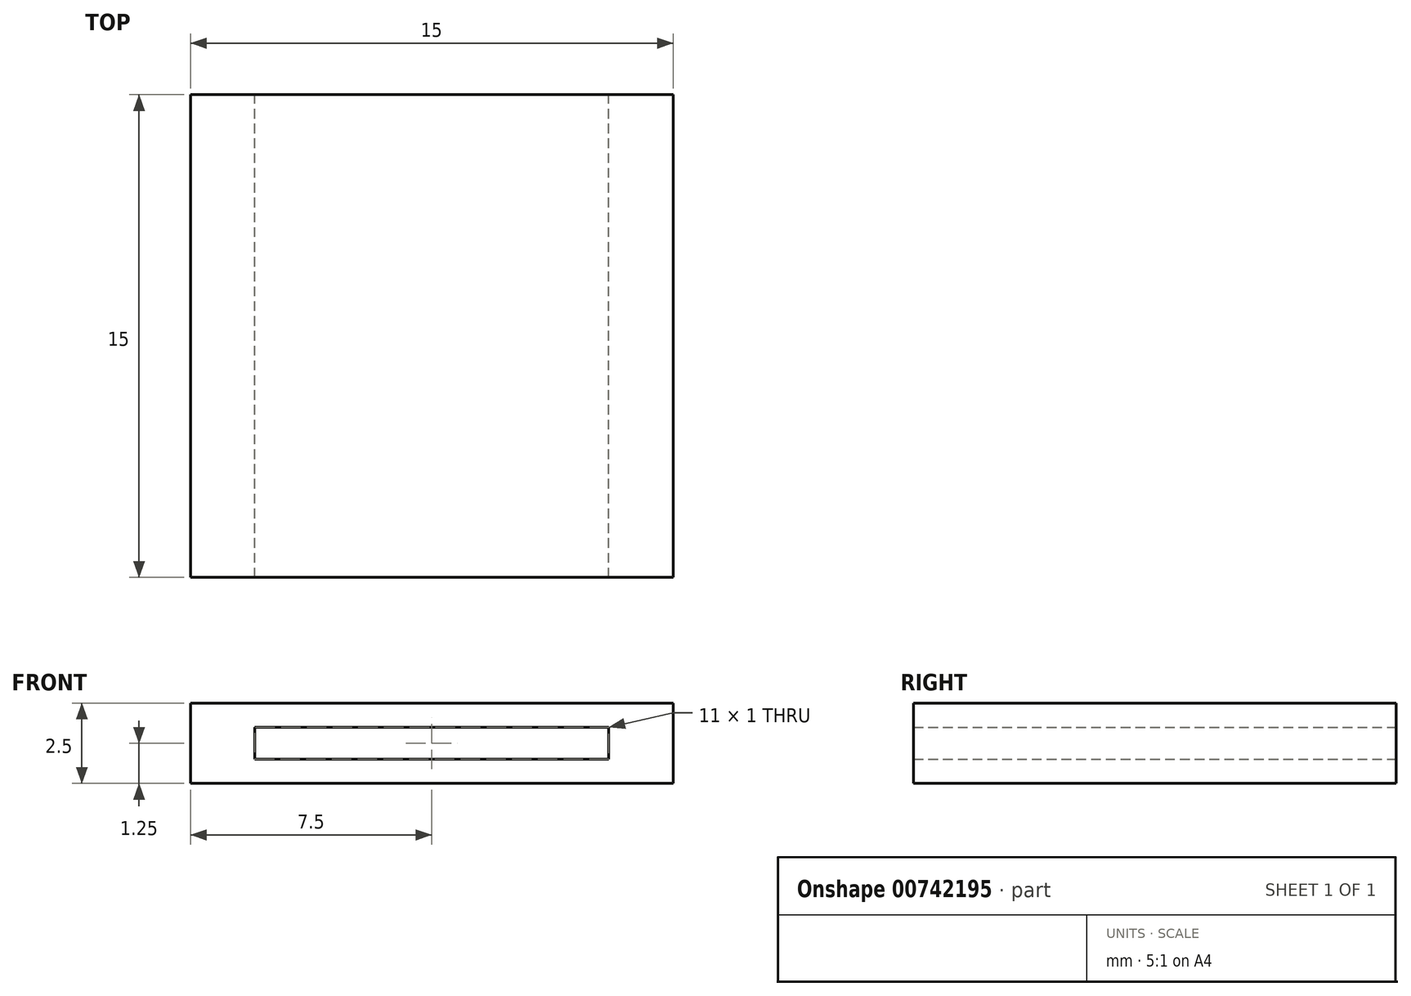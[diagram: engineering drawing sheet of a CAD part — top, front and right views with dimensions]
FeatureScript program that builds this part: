
annotation { "Feature Type Name" : "Feature", "Feature Type Description" : "" }
export const myFeature = defineFeature(function(context is Context, id is Id, definition is map)
    precondition{}
    {
        {
            var Q0;
            Q0=qCreatedBy(makeId("Front.planeOp"),FACE);
            var sketch = newSketch(context, id + "F0", { "sketchPlane" : qUnion([Q0])});
            skLineSegment(sketch, "E0.bottom", {"start": v(0, 0) * mm, "end": v(15, 0) * mm});
            skLineSegment(sketch, "E0.top", {"start": v(0, 2.5) * mm, "end": v(15, 2.5) * mm});
            skLineSegment(sketch, "E0.left", {"start": v(0, 0) * mm, "end": v(0, 2.5) * mm});
            skLineSegment(sketch, "E0.right", {"start": v(15, 0) * mm, "end": v(15, 2.5) * mm});
            skLineSegment(sketch, "E1.bottom", {"start": v(2, 1.75) * mm, "end": v(13, 1.75) * mm});
            skLineSegment(sketch, "E1.top", {"start": v(2, 0.75) * mm, "end": v(13, 0.75) * mm});
            skLineSegment(sketch, "E1.left", {"start": v(2, 1.75) * mm, "end": v(2, 0.75) * mm});
            skLineSegment(sketch, "E1.right", {"start": v(13, 1.75) * mm, "end": v(13, 0.75) * mm});
            skSolve(sketch);
        }
        {
            var Q0;
            Q0 = qSketchRegion(id + "F0", true);
            extrude(context, id + "F1", {"entities" : qUnion([Q0]), "depth" : 15 * mm, "offsetDistance" : 25 * mm});
        }
    });
